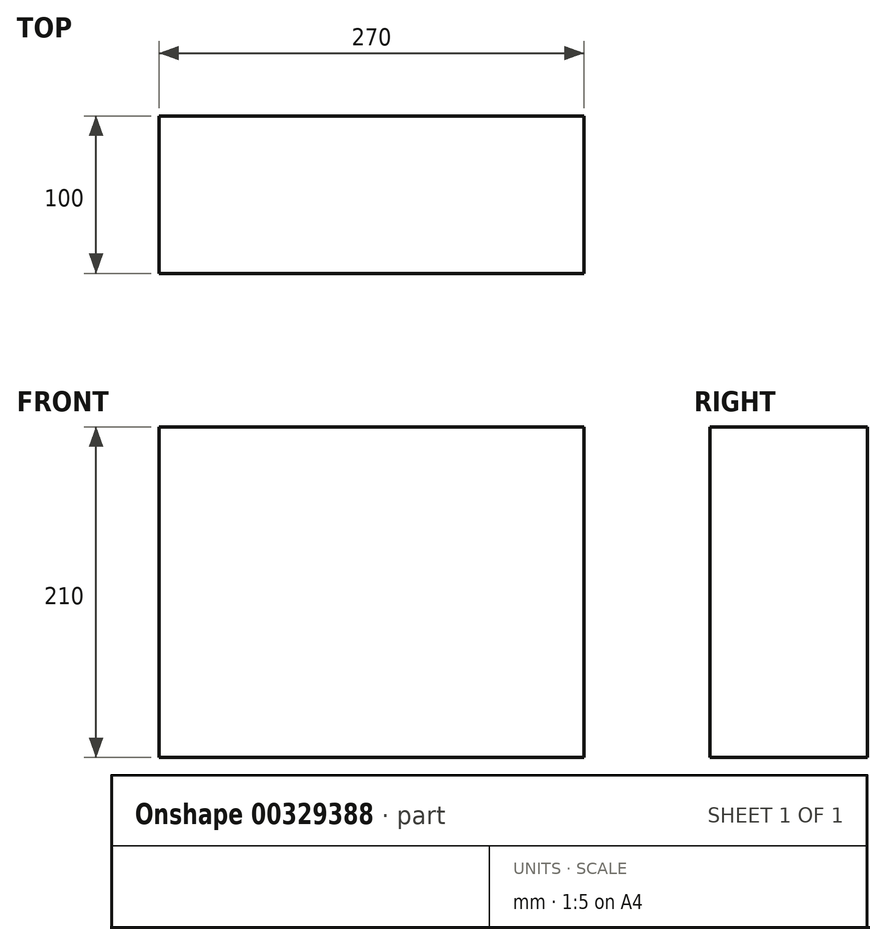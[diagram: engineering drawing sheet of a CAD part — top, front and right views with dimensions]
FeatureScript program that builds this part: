
annotation { "Feature Type Name" : "Feature", "Feature Type Description" : "" }
export const myFeature = defineFeature(function(context is Context, id is Id, definition is map)
    precondition{}
    {
        {
            var Q0;
            Q0=qCreatedBy(makeId("Front.planeOp"),FACE);
            var sketch = newSketch(context, id + "F0", { "sketchPlane" : qUnion([Q0])});
            skLineSegment(sketch, "E0.bottom", {"start": v(-135, 105) * mm, "end": v(135, 105) * mm});
            skLineSegment(sketch, "E0.top", {"start": v(-135, -105) * mm, "end": v(135, -105) * mm});
            skLineSegment(sketch, "E0.left", {"start": v(-135, 105) * mm, "end": v(-135, -105) * mm});
            skLineSegment(sketch, "E0.right", {"start": v(135, 105) * mm, "end": v(135, -105) * mm});
            skLineSegment(sketch, "E1", {"start": v(-135, -105) * mm, "end": v(135, 105) * mm, "construction": true});
            skSolve(sketch);
        }
        {
            var Q0;
            Q0 = qSketchRegion(id + "F0", true);
            extrude(context, id + "F1", {"entities" : qUnion([Q0]), "depth" : 100 * mm});
        }
    });
